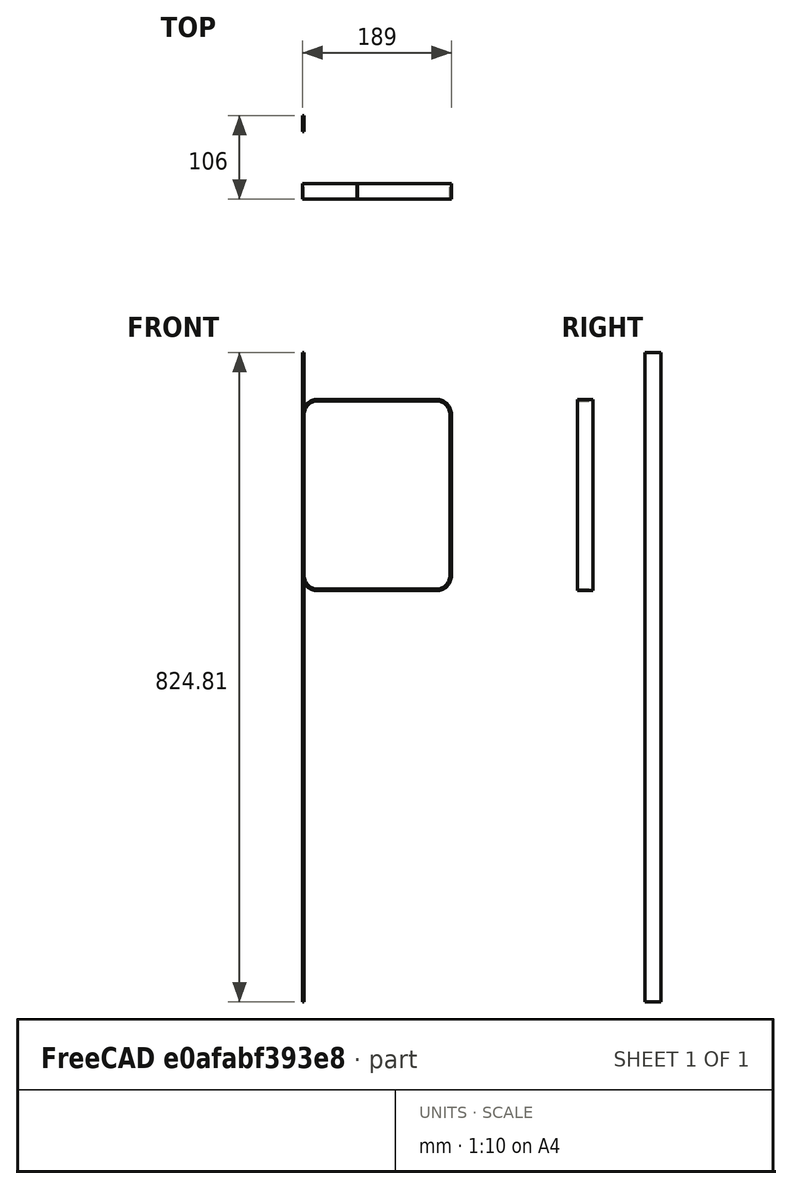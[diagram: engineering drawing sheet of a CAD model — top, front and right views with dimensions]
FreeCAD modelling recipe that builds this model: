
FCSTD DOCUMENT  (FreeCAD 0.17R13528 (Git))
Label: frame
License: All rights reserved
LicenseURL: http://en.wikipedia.org/wiki/All_rights_reserved
objects: PartDesign::FeaturePython×4, Sketcher::SketchObject×2, Spreadsheet::Sheet×1, Part::Feature×1, App::Part×1, PartDesign::Body×1, PartDesign::Pad×1
note: 10 computed .brp shape members not serialized (recipe doc carries the construction recipe); baked Part::Feature solids carry a one-line shape summary decoded from their .brp

FEATURE [Spreadsheet::Sheet] Spreadsheet
  cells = A1=bend_radius; B1=17; A2=Height; B2=205; A3=Width; B3=151
FEATURE [Part::Feature] Unfold
  Placement = pos=(0,86,0) rot=(0,0,1;0rad)
  shape: bbox 2 x 20 x 824.8 mm, 6 faces (baked)
FEATURE [Sketcher::SketchObject] Sketch001  label="Unfold_Sketch"
  Placement = pos=(0,86,0) rot=(0,0,1;0rad)
  sketch-geometry (8):
    g0: LineSegment StartX=-764.364 StartY=-20 StartZ=0 EndX=-764.364 EndY=0 EndZ=0
    g1: LineSegment StartX=60.4545 StartY=-20 StartZ=0 EndX=-764.364 EndY=-20 EndZ=0
    g2: LineSegment StartX=60.4545 StartY=0 StartZ=0 EndX=60.4545 EndY=-20 EndZ=0
    g3: LineSegment StartX=-764.364 StartY=0 StartZ=0 EndX=60.4545 EndY=0 EndZ=0
    g4: LineSegment StartX=-650.136 StartY=-20 StartZ=0 EndX=-650.136 EndY=0 EndZ=0
    g5: LineSegment StartX=-416.682 StartY=-20 StartZ=0 EndX=-416.682 EndY=0 EndZ=0
    g6: LineSegment StartX=-237.227 StartY=-20 StartZ=0 EndX=-237.227 EndY=0 EndZ=0
    g7: LineSegment StartX=-3.77274 StartY=-20 StartZ=0 EndX=-3.77274 EndY=0 EndZ=0
FEATURE [App::Part] Part
  Group = -> [Body]
  License = CC BY 3.0
  LicenseURL = http://creativecommons.org/licenses/by/3.0/
  Origin = -> Origin
FEATURE [Sketcher::SketchObject] Sketch
  MapMode = 2
  Support = -> [Part]
  sketch-geometry (4):
    g0: LineSegment StartX=0 StartY=0 StartZ=0 EndX=100 EndY=0 EndZ=0
    g1: LineSegment StartX=100 StartY=0 StartZ=0 EndX=100 EndY=20 EndZ=0
    g2: LineSegment StartX=100 StartY=20 StartZ=0 EndX=0 EndY=20 EndZ=0
    g3: LineSegment StartX=0 StartY=20 StartZ=0 EndX=0 EndY=0 EndZ=0
  constraints (11):
    c: Coincident(g0,g1)
    c: Coincident(g1,g2)
    c: Coincident(g2,g3)
    c: Coincident(g3,g0)
    c: Horizontal(g0)
    c: Horizontal(g2)
    c: Vertical(g1)
    c: Vertical(g3)
    c: Coincident(g0,g-1)
    c: DistanceY(g3,g3) = 20
    c: DistanceX(g0,g0) = 100
FEATURE [PartDesign::Body] Body
  Group = -> [Sketch,Pad,Bend,Bend001,Bend002,Bend003]
  Origin = -> Origin001
  Tip = -> Bend003
FEATURE [PartDesign::Pad] Pad
  Length = 2
  Length2 = 100
  Midplane = true
  Profile = -> Sketch
  Type = 0
FEATURE [PartDesign::FeaturePython] Bend  # WARN: FeaturePython — macro-defined, semantics opaque (R4)
  AutoMiter = true
  BaseFeature = -> Pad
  BendType = 0
  LengthList = [205]
  RelifFactor = 0.7
  UseRelifFactor = false
  angle = 90
  baseObject = -> Pad [Face2]
  bendAList = [90]
  extend1 = 0
  extend2 = 0
  gap1 = 0
  gap2 = 0
  invert = true
  kfactor = 0.5
  length = 205
  miterangle1 = 0
  miterangle2 = 0
  offset = 0
  radius = 17
  reliefType = 0
  reliefd = 1
  reliefw = 0.8
  sketchflip = false
  sketchinvert = false
  unfold = false
  expr: length = Spreadsheet.B2
  expr: radius = Spreadsheet.B1
FEATURE [PartDesign::FeaturePython] Bend001  # WARN: FeaturePython — macro-defined, semantics opaque (R4)
  AutoMiter = true
  BaseFeature = -> Bend
  BendType = 0
  LengthList = [151]
  RelifFactor = 0.7
  UseRelifFactor = false
  angle = 90
  baseObject = -> Bend [Face3]
  bendAList = [90]
  extend1 = 0
  extend2 = 0
  gap1 = 0
  gap2 = 0
  invert = true
  kfactor = 0.5
  length = 151
  miterangle1 = 0
  miterangle2 = 0
  offset = 0
  radius = 17
  reliefType = 0
  reliefd = 1
  reliefw = 0.8
  sketchflip = false
  sketchinvert = false
  unfold = false
  expr: length = Spreadsheet.B3
  expr: radius = Spreadsheet.B1
FEATURE [PartDesign::FeaturePython] Bend002  # WARN: FeaturePython — macro-defined, semantics opaque (R4)
  AutoMiter = true
  BaseFeature = -> Bend001
  BendType = 0
  LengthList = [205]
  RelifFactor = 0.7
  UseRelifFactor = false
  angle = 90
  baseObject = -> Bend001 [Face3]
  bendAList = [90]
  extend1 = 0
  extend2 = 0
  gap1 = 0
  gap2 = 0
  invert = true
  kfactor = 0.5
  length = 205
  miterangle1 = 0
  miterangle2 = 0
  offset = 0
  radius = 17
  reliefType = 0
  reliefd = 1
  reliefw = 0.8
  sketchflip = false
  sketchinvert = false
  unfold = false
  expr: length = Spreadsheet.B2
  expr: radius = Spreadsheet.B1
FEATURE [PartDesign::FeaturePython] Bend003  # WARN: FeaturePython — macro-defined, semantics opaque (R4)
  AutoMiter = true
  BaseFeature = -> Bend002
  BendType = 0
  LengthList = [50]
  RelifFactor = 0.7
  UseRelifFactor = false
  angle = 90
  baseObject = -> Bend002 [Face3]
  bendAList = [90]
  extend1 = 0
  extend2 = 0
  gap1 = 0
  gap2 = 0
  invert = true
  kfactor = 0.5
  length = 50
  miterangle1 = 0
  miterangle2 = 0
  offset = 0
  radius = 17
  reliefType = 0
  reliefd = 1
  reliefw = 0.8
  sketchflip = false
  sketchinvert = false
  unfold = false
  expr: radius = Spreadsheet.B1
